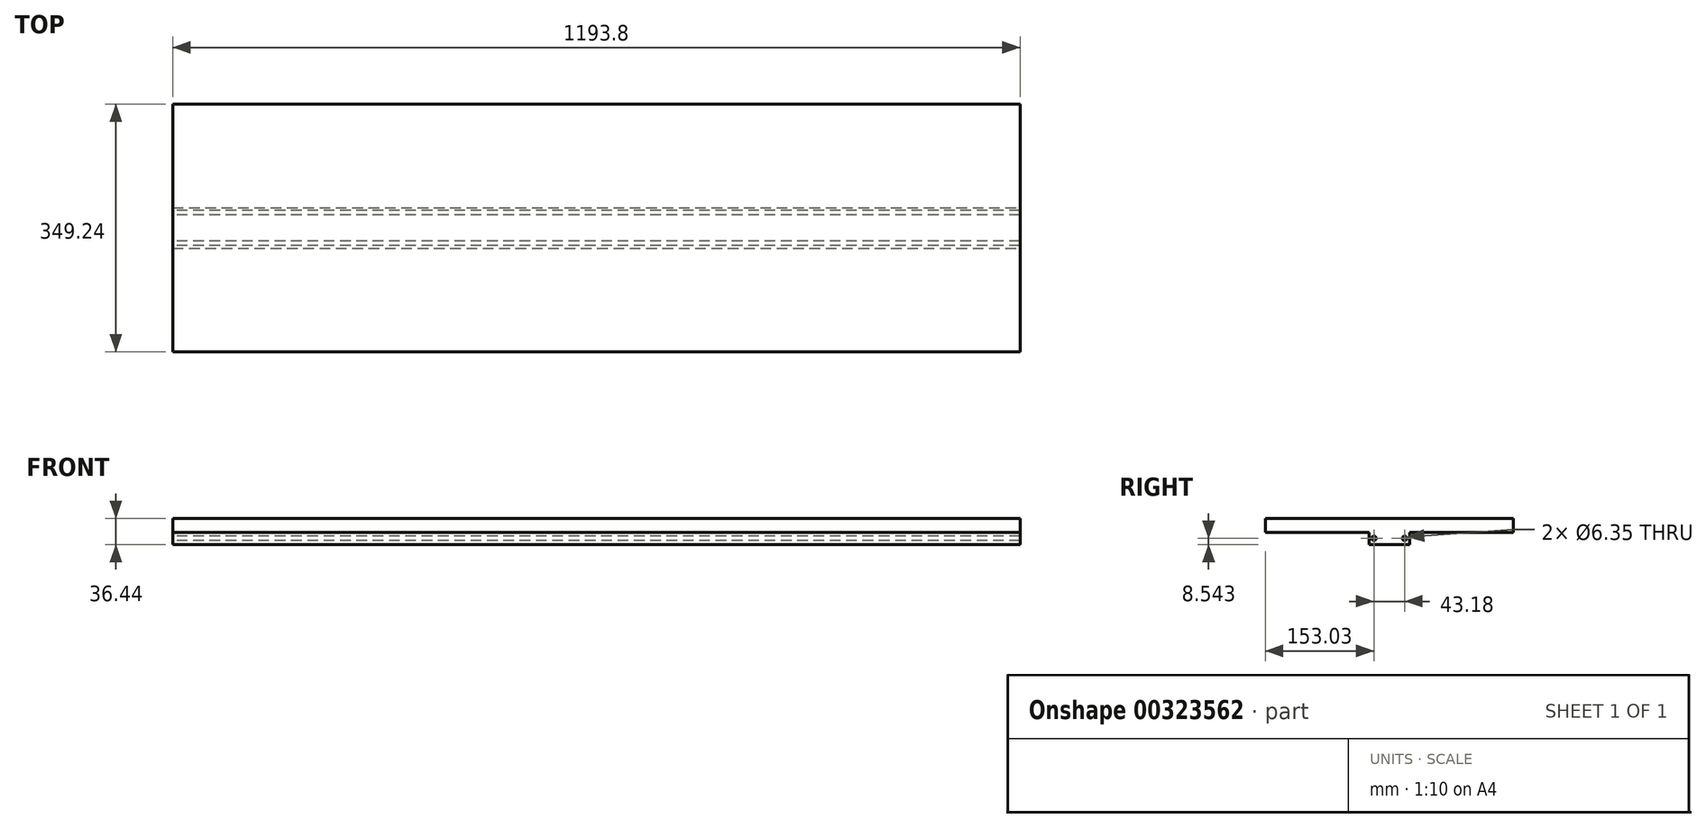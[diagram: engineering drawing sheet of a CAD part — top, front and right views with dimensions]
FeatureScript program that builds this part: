
annotation { "Feature Type Name" : "Feature", "Feature Type Description" : "" }
export const myFeature = defineFeature(function(context is Context, id is Id, definition is map)
    precondition{}
    {
        {
            var Q0;
            Q0=qCreatedBy(makeId("Top.planeOp"),FACE);
            var sketch = newSketch(context, id + "F0", { "sketchPlane" : qUnion([Q0])});
            skLineSegment(sketch, "E0.bottom", {"start": v(-596.9, 174.63) * mm, "end": v(596.9, 174.63) * mm});
            skLineSegment(sketch, "E0.top", {"start": v(-596.9, -174.63) * mm, "end": v(596.9, -174.63) * mm});
            skLineSegment(sketch, "E0.left", {"start": v(-596.9, 174.63) * mm, "end": v(-596.9, -174.63) * mm});
            skLineSegment(sketch, "E0.right", {"start": v(596.9, 174.63) * mm, "end": v(596.9, -174.63) * mm});
            skPoint(sketch, "E0.middle", {"position": v(0, 0) * mm});
            skSolve(sketch);
        }
        {
            var Q0;
            Q0=makeQuery(id+"F0.imprint","IMPRINT",FACE,{"disambiguationData":[TD([[makeQuery(id+"F0.imprint","IMPRINT",EDGE,{"derivedFrom":sQuery(id+"F0.wireOp",EDGE,"E0.bottom")}),-1.0]])]});
            extrude(context, id + "F1", {"entities" : qUnion([Q0]), "depth" : 19.35 * mm});
        }
        {
            var Q0;
            Q0=makeQuery(id+"F1.opExtrude","CAP_FACE",FACE,{"disambiguationData":[OSD([sQuery(id+"F0.wireOp",EDGE,"E0.bottom"),sQuery(id+"F0.wireOp",EDGE,"E0.top"),sQuery(id+"F0.wireOp",EDGE,"E0.left"),sQuery(id+"F0.wireOp",EDGE,"E0.right")])],"isStart":true});
            var sketch = newSketch(context, id + "F2", { "sketchPlane" : qUnion([Q0])});
            skLineSegment(sketch, "E1.bottom", {"start": v(-596.9, 28.57) * mm, "end": v(596.9, 28.57) * mm});
            skLineSegment(sketch, "E1.top", {"start": v(-596.9, -28.58) * mm, "end": v(596.9, -28.58) * mm});
            skLineSegment(sketch, "E1.left", {"start": v(-596.9, 28.57) * mm, "end": v(-596.9, -28.58) * mm});
            skLineSegment(sketch, "E1.right", {"start": v(596.9, 28.57) * mm, "end": v(596.9, -28.58) * mm});
            skPoint(sketch, "E1.middle", {"position": v(0, 0) * mm});
            skSolve(sketch);
        }
        {
            var Q0;
            Q0 = qSketchRegion(id + "F2", true);
            extrude(context, id + "F3", {"entities" : qUnion([Q0]), "operationType" : NewBodyOperationType.ADD, "depth" : 17.1 * mm});
        }
        {
            var Q0;
            Q0=makeQuery(id+"F3.boolean.opBoolean","MERGE",FACE,{"derivedFrom":[makeQuery(id+"F1.opExtrude","SWEPT_FACE",FACE,{"disambiguationData":[OSD([sQuery(id+"F0.wireOp",EDGE,"E0.left")])]}),makeQuery(id+"F3.opExtrude","SWEPT_FACE",FACE,{"disambiguationData":[OSD([sQuery(id+"F2.wireOp",EDGE,"E1.left")])]})]});
            var sketch = newSketch(context, id + "F4", { "sketchPlane" : qUnion([Q0])});
            skPoint(sketch, "E2", {"position": v(0, -17.1) * mm});
            skPoint(sketch, "E3", {"position": v(-28.58, -8.55) * mm});
            skPoint(sketch, "E4", {"position": v(28.57, -8.55) * mm});
            skPoint(sketch, "E5", {"position": v(21.59, -8.55) * mm});
            skPoint(sketch, "E6", {"position": v(-21.59, -8.55) * mm});
            skPoint(sketch, "E7", {"position": v(0, -8.55) * mm});
            skSolve(sketch);
        }
        {
            var Q0;
            Q0=sQuery(id+"F4.wireOp",VERTEX,"E6");
            var Q1;
            Q1=sQuery(id+"F4.wireOp",VERTEX,"E5");
            var Q2;
            Q2=makeQuery(id+"F1.opExtrude","SWEPT_BODY",BODY,{"disambiguationData":[OSD([sQuery(id+"F0.wireOp",EDGE,"E0.bottom"),sQuery(id+"F0.wireOp",EDGE,"E0.top"),sQuery(id+"F0.wireOp",EDGE,"E0.left"),sQuery(id+"F0.wireOp",EDGE,"E0.right")])]});
            hole(context, id + "F5", {"style" : HoleStyle.SIMPLE, "endStyle" : HoleEndStyle.THROUGH, "holeDiameter" : 6.35 * mm, "tappedDepth" : 12.7 * mm, "tapClearance" : 3, "locations" : qUnion([Q0, Q1]), "scope" : qUnion([Q2])});
        }
    });
